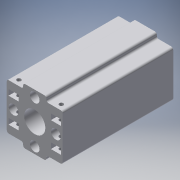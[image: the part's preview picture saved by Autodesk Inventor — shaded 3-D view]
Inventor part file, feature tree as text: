
AUTODESK INVENTOR PART (.ipt)
format: ipt  version: 2016 (Build 200138000, 138)  size: 288,768 bytes
history: native  units: in
note: dims shown in document units (in); Inventor stores cm internally (conversion verified against a paired STEP export)
features: projected_geometry x6, extrude x4, sketch x4, plane x2, mirror x2, fillet x1, other x1, imported_body x1
ambient origin geometry x8: Origin, YZ Plane, XZ Plane, XY Plane, X Axis, Y Axis, Z Axis, Center Point
bodies: Body1 (feature_tree)
feature tree (21):
  fillet  "Fillet1"  Radius=0.1575in
  other  "headnickholder.ipt1"
  extrude  "Extrusion1"  Depth=0.1181in
  extrude  "Extrusion2"  Depth=0.0787in TaperAngle=0.0deg
  plane  "Work Plane1"
  plane  "Work Plane2"
  mirror  "Mirror1"
  mirror  "Mirror2"
  extrude  "Extrusion3"  Depth=0.1181in TaperAngle=0.0deg
  extrude  "Extrusion4"  Depth=0.7874in TaperAngle=0.0deg
  imported_body  "Base1"
  sketch  "Sketch1"  dims[d1=0.1024in d2=0.1181in]
  projected_geometry  "Projected Loop1"
  sketch  "Sketch2"  dims[d3=0.1024in d4=0.0787in d5=0.0in]
  sketch  "Sketch3"  dims[d6=0.1024in d7=0.1181in d8=0.0in]
  projected_geometry  "Projected Loop2"
  sketch  "Sketch4"  dims[d9=1.7874in d10=0.0in d11=0.7874in d12=0.0in]
  projected_geometry  "Projected Loop3"
  projected_geometry  "Projected Loop4"
  projected_geometry  "Projected Loop5"
  projected_geometry  "Projected Loop6"
